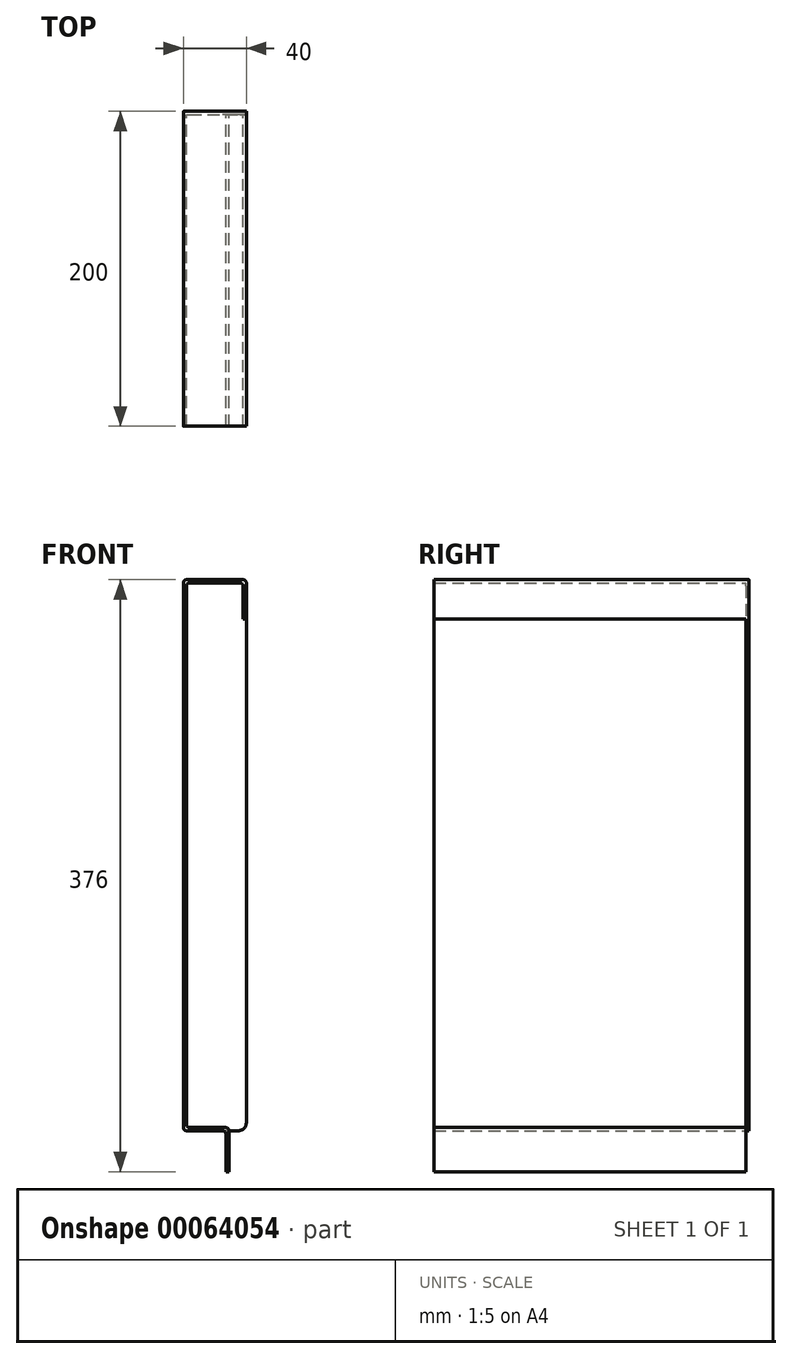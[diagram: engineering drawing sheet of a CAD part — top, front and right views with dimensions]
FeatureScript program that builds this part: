
annotation { "Feature Type Name" : "Feature", "Feature Type Description" : "" }
export const myFeature = defineFeature(function(context is Context, id is Id, definition is map)
    precondition{}
    {
        {
            var Q0;
            Q0=qCreatedBy(makeId("Front.planeOp"),FACE);
            var sketch = newSketch(context, id + "F0", { "sketchPlane" : qUnion([Q0])});
            skLineSegment(sketch, "E0", {"start": v(0, 0) * mm, "end": v(0, -350) * mm});
            skLineSegment(sketch, "E1", {"start": v(0, -350) * mm, "end": v(27, -350) * mm});
            skLineSegment(sketch, "E2", {"start": v(27, -350) * mm, "end": v(27, -376) * mm});
            skLineSegment(sketch, "E3", {"start": v(0, 0) * mm, "end": v(40, 0) * mm});
            skLineSegment(sketch, "E4", {"start": v(40, 0) * mm, "end": v(40, -25) * mm});
            skLineSegment(sketch, "E5.0", {"start": v(38, -2) * mm, "end": v(38, -25) * mm});
            skLineSegment(sketch, "E5.1", {"start": v(29, -348) * mm, "end": v(29, -376) * mm});
            skLineSegment(sketch, "E5.2", {"start": v(2, -348) * mm, "end": v(29, -348) * mm});
            skLineSegment(sketch, "E5.3", {"start": v(2, -2) * mm, "end": v(2, -348) * mm});
            skLineSegment(sketch, "E5.4", {"start": v(2, -2) * mm, "end": v(38, -2) * mm});
            skLineSegment(sketch, "E6", {"start": v(38, -25) * mm, "end": v(40, -25) * mm});
            skLineSegment(sketch, "E7", {"start": v(27, -376) * mm, "end": v(29, -376) * mm});
            skSolve(sketch);
        }
        {
            var Q0;
            Q0=qCreatedBy(makeId("Top.planeOp"),FACE);
            var sketch = newSketch(context, id + "F1", { "sketchPlane" : qUnion([Q0])});
            skLineSegment(sketch, "E8", {"start": v(0, 0) * mm, "end": v(0, 198) * mm});
            skSolve(sketch);
        }
        {
            var Q0;
            Q0=qSketchRegion(id+"F0",true);
            var Q1;
            Q1=qConstructionFilter(qBodyType(qCreatedBy(id+"F1",EDGE),BodyType.WIRE),ConstructionObject.NO);
            sweep(context, id + "F2", {"profiles" : qUnion([Q0]), "path" : qUnion([Q1])});
        }
        {
            var Q0;
            Q0=makeQuery(id+"F2.opSweep","CAP_FACE",FACE,{"disambiguationData":[OSD([sQuery(id+"F0.wireOp",EDGE,"E0"),sQuery(id+"F0.wireOp",EDGE,"E1"),sQuery(id+"F0.wireOp",EDGE,"E2"),sQuery(id+"F0.wireOp",EDGE,"E3"),sQuery(id+"F0.wireOp",EDGE,"E4"),sQuery(id+"F0.wireOp",EDGE,"E5.0"),sQuery(id+"F0.wireOp",EDGE,"E5.1"),sQuery(id+"F0.wireOp",EDGE,"E5.2"),sQuery(id+"F0.wireOp",EDGE,"E5.3"),sQuery(id+"F0.wireOp",EDGE,"E5.4"),sQuery(id+"F0.wireOp",EDGE,"E6"),sQuery(id+"F0.wireOp",EDGE,"E7"),sQuery(id+"F1.wireOp",VERTEX,"E8.end")])],"isStart":false});
            var sketch = newSketch(context, id + "F3", { "sketchPlane" : qUnion([Q0])});
            skLineSegment(sketch, "E9.0", {"start": v(0, -350) * mm, "end": v(0, 0) * mm});
            skLineSegment(sketch, "E10.0", {"start": v(-40, 0) * mm, "end": v(0, 0) * mm});
            skLineSegment(sketch, "E11.0", {"start": v(-40, -25) * mm, "end": v(-40, 0) * mm});
            skLineSegment(sketch, "E12.0", {"start": v(-40, -25) * mm, "end": v(-40, -345) * mm});
            skArc(sketch, "E13.0", {"start": v(-35, -350) * mm, "mid": v(-38.54, -348.54) * mm, "end": v(-40, -345) * mm});
            skLineSegment(sketch, "E14.0", {"start": v(-35, -350) * mm, "end": v(-29, -350) * mm});
            skLineSegment(sketch, "E15.0", {"start": v(-27, -350) * mm, "end": v(0, -350) * mm});
            skLineSegment(sketch, "E16", {"start": v(-29, -350) * mm, "end": v(-27, -350) * mm});
            skSolve(sketch);
        }
        {
            var Q0;
            Q0=qSketchRegion(id+"F3",true);
            extrude(context, id + "F4", {"entities" : qUnion([Q0]), "operationType" : NewBodyOperationType.ADD, "depth" : 2 * mm});
        }
        {
            var Q0;
            Q0=makeQuery(id+"F4.boolean.opBoolean","MERGE",EDGE,{"derivedFrom":[makeQuery(id+"F2.opSweep","SWEPT_EDGE",EDGE,{"disambiguationData":[OSD([sQuery(id+"F0.wireOp",EDGE,"E0"),sQuery(id+"F0.wireOp",EDGE,"E3"),sQuery(id+"F1.wireOp",EDGE,"E8")])]}),makeQuery(id+"F4.opExtrude","SWEPT_EDGE",EDGE,{"disambiguationData":[OSD([sQuery(id+"F3.wireOp",EDGE,"E9.0"),sQuery(id+"F3.wireOp",EDGE,"E10.0")])]})]});
            var Q1;
            Q1=makeQuery(id+"F4.boolean.opBoolean","MERGE",EDGE,{"derivedFrom":[makeQuery(id+"F2.opSweep","SWEPT_EDGE",EDGE,{"disambiguationData":[OSD([sQuery(id+"F0.wireOp",EDGE,"E3"),sQuery(id+"F0.wireOp",EDGE,"E4"),sQuery(id+"F1.wireOp",EDGE,"E8")])]}),makeQuery(id+"F4.opExtrude","SWEPT_EDGE",EDGE,{"disambiguationData":[OSD([sQuery(id+"F3.wireOp",EDGE,"E10.0"),sQuery(id+"F3.wireOp",EDGE,"E11.0")])]})]});
            var Q2;
            Q2=makeQuery(id+"F2.opSweep","SWEPT_EDGE",EDGE,{"disambiguationData":[OSD([sQuery(id+"F0.wireOp",EDGE,"E5.2"),sQuery(id+"F0.wireOp",EDGE,"E5.3"),sQuery(id+"F1.wireOp",EDGE,"E8")])]});
            var Q3;
            Q3=makeQuery(id+"F2.opSweep","SWEPT_EDGE",EDGE,{"disambiguationData":[OSD([sQuery(id+"F0.wireOp",EDGE,"E5.1"),sQuery(id+"F0.wireOp",EDGE,"E5.2"),sQuery(id+"F1.wireOp",EDGE,"E8")])]});
            var Q4;
            Q4=makeQuery(id+"F4.boolean.opBoolean","MERGE",EDGE,{"derivedFrom":[makeQuery(id+"F2.opSweep","SWEPT_EDGE",EDGE,{"disambiguationData":[OSD([sQuery(id+"F0.wireOp",EDGE,"E0"),sQuery(id+"F0.wireOp",EDGE,"E1"),sQuery(id+"F1.wireOp",EDGE,"E8")])]}),makeQuery(id+"F4.opExtrude","SWEPT_EDGE",EDGE,{"disambiguationData":[OSD([sQuery(id+"F3.wireOp",EDGE,"E9.0"),sQuery(id+"F3.wireOp",EDGE,"E15.0")])]})]});
            var Q5;
            Q5=makeQuery(id+"F2.opSweep","SWEPT_EDGE",EDGE,{"disambiguationData":[OSD([sQuery(id+"F0.wireOp",EDGE,"E1"),sQuery(id+"F0.wireOp",EDGE,"E2"),sQuery(id+"F1.wireOp",EDGE,"E8")])]});
            var Q6;
            Q6=makeQuery(id+"F2.opSweep","SWEPT_EDGE",EDGE,{"disambiguationData":[OSD([sQuery(id+"F0.wireOp",EDGE,"E5.0"),sQuery(id+"F0.wireOp",EDGE,"E5.4"),sQuery(id+"F1.wireOp",EDGE,"E8")])]});
            var Q7;
            Q7=makeQuery(id+"F2.opSweep","SWEPT_EDGE",EDGE,{"disambiguationData":[OSD([sQuery(id+"F0.wireOp",EDGE,"E5.3"),sQuery(id+"F0.wireOp",EDGE,"E5.4"),sQuery(id+"F1.wireOp",EDGE,"E8")])]});
            fillet(context, id + "F5", {"entities" : qUnion([Q0, Q1, Q2, Q3, Q4, Q5, Q6, Q7]), "radius" : 2 * mm, "tangentPropagation" : true, "allowEdgeOverflow" : false});
        }
    });
